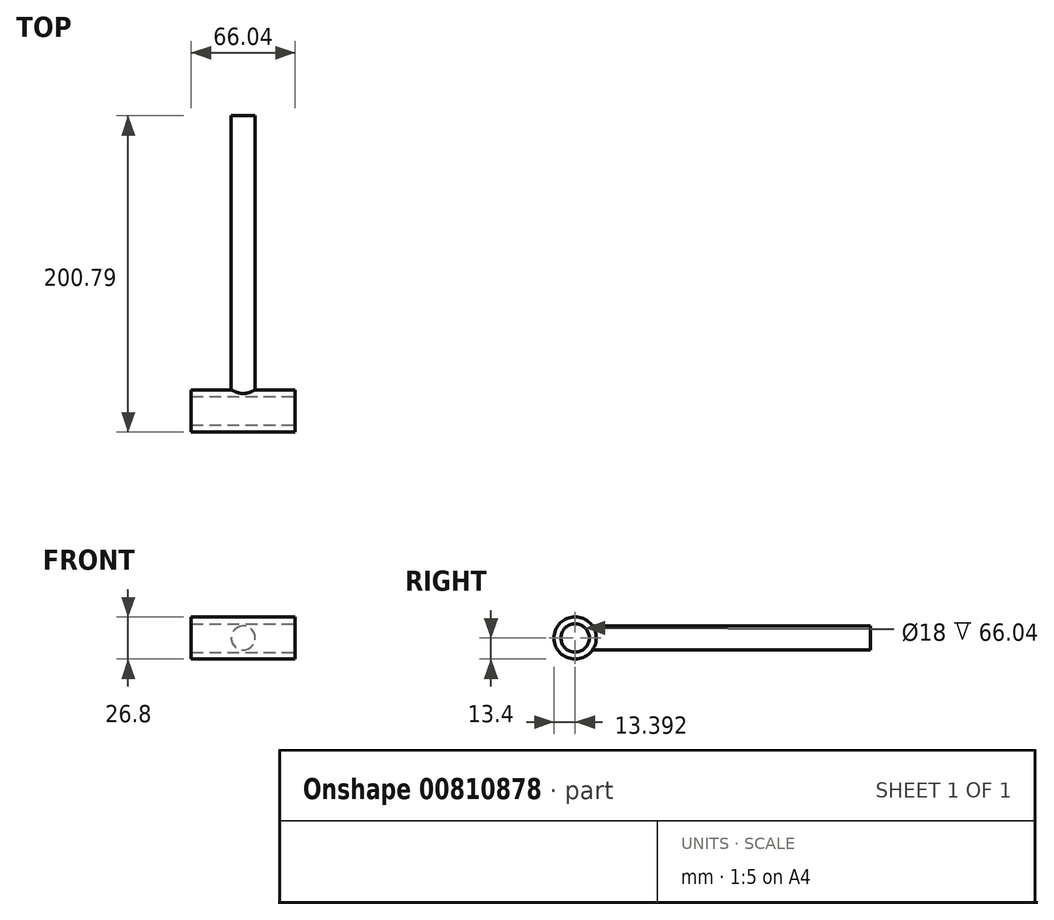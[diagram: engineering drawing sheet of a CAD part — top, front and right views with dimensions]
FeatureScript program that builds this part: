
annotation { "Feature Type Name" : "Feature", "Feature Type Description" : "" }
export const myFeature = defineFeature(function(context is Context, id is Id, definition is map)
    precondition{}
    {
        {
            var Q0;
            Q0=qCreatedBy(makeId("Front.planeOp"),FACE);
            var sketch = newSketch(context, id + "F0", { "sketchPlane" : qUnion([Q0])});
            skCircle(sketch, "E0", {"center": v(0, 0) * mm, "radius": 7.62 * mm});
            skSolve(sketch);
        }
        {
            var Q0;
            Q0 = qSketchRegion(id + "F0", true);
            extrude(context, id + "F1", {"entities" : qUnion([Q0]), "depth" : 177.8 * mm, "offsetDistance" : 25.4 * mm});
        }
        {
            var Q0;
            Q0=qCreatedBy(makeId("Right.planeOp"),FACE);
            var sketch = newSketch(context, id + "F2", { "sketchPlane" : qUnion([Q0])});
            skCircle(sketch, "E1", {"center": v(-187.4, 0) * mm, "radius": 13.4 * mm});
            skSolve(sketch);
        }
        {
            var Q0;
            Q0 = qSketchRegion(id + "F2", true);
            extrude(context, id + "F3", {"entities" : qUnion([Q0]), "operationType" : NewBodyOperationType.ADD, "depth" : 66.04 * mm, "offsetDistance" : 25.4 * mm, "symmetric" : true});
        }
        {
            var Q0;
            Q0=makeQuery(id+"F3.opExtrude","CAP_FACE",FACE,{"disambiguationData":[OSD([sQuery(id+"F2.wireOp",EDGE,"E1")])],"isStart":false});
            var sketch = newSketch(context, id + "F4", { "sketchPlane" : qUnion([Q0])});
            skCircle(sketch, "E2", {"center": v(-187.4, 0) * mm, "radius": 9 * mm});
            skSolve(sketch);
        }
        {
            var Q0;
            Q0 = qSketchRegion(id + "F4", true);
            extrude(context, id + "F5", {"entities" : qUnion([Q0]), "operationType" : NewBodyOperationType.REMOVE, "oppositeDirection" : true, "depth" : 83.31 * mm, "offsetDistance" : 25.4 * mm});
        }
    });
